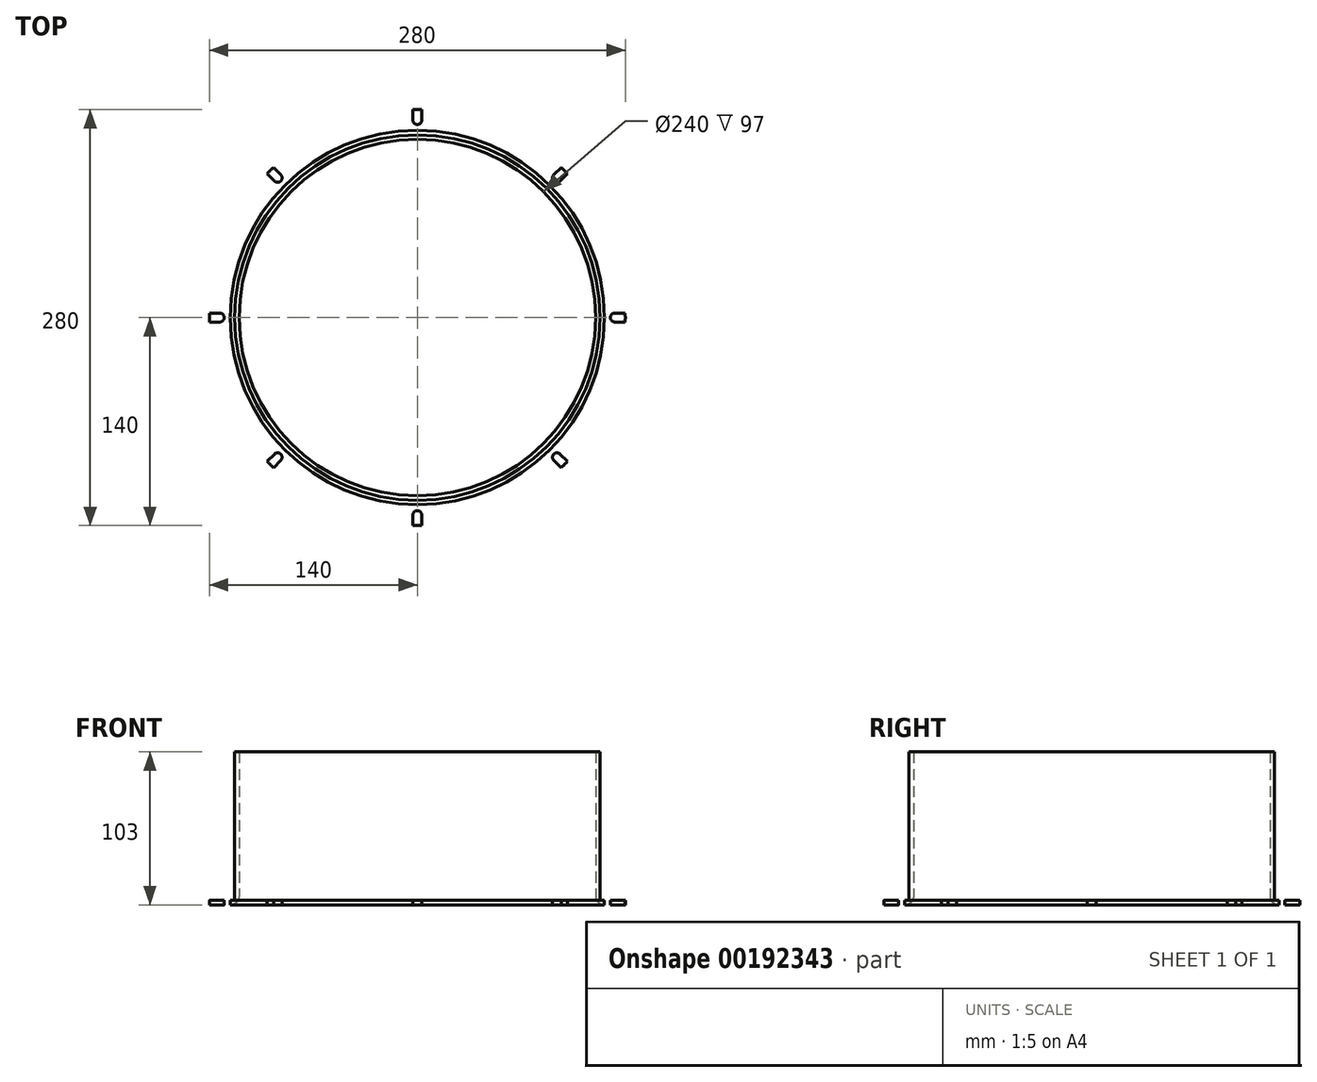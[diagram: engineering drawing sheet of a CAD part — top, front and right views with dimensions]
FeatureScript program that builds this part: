
annotation { "Feature Type Name" : "Feature", "Feature Type Description" : "" }
export const myFeature = defineFeature(function(context is Context, id is Id, definition is map)
    precondition{}
    {
        {
            var Q0;
            Q0=qCreatedBy(makeId("Top.planeOp"),FACE);
            var sketch = newSketch(context, id + "F0", { "sketchPlane" : qUnion([Q0])});
            skCircle(sketch, "E0", {"center": v(0, 0) * mm, "radius": 140 * mm});
            skCircle(sketch, "E1.0", {"center": v(0, 0) * mm, "radius": 120 * mm});
            skSolve(sketch);
        }
        {
            var Q0;
            Q0=makeQuery(id+"F0.imprint","IMPRINT",FACE,{"disambiguationData":[TD([[makeQuery(id+"F0.imprint","IMPRINT",EDGE,{"derivedFrom":sQuery(id+"F0.wireOp",EDGE,"E0")}),1.0]])]});
            extrude(context, id + "F1", {"entities" : qUnion([Q0]), "depth" : 3 * mm});
        }
        {
            var Q0;
            Q0=makeQuery(id+"F1.opExtrude","CAP_FACE",FACE,{"disambiguationData":[OSD([sQuery(id+"F0.wireOp",EDGE,"E0"),sQuery(id+"F0.wireOp",EDGE,"E1.0")])],"isStart":false});
            var sketch = newSketch(context, id + "F2", { "sketchPlane" : qUnion([Q0])});
            skCircle(sketch, "E2.0", {"center": v(0, 0) * mm, "radius": 120 * mm});
            skCircle(sketch, "E3.0", {"center": v(0, 0) * mm, "radius": 123 * mm});
            skSolve(sketch);
        }
        {
            var Q0;
            Q0=makeQuery(id+"F2.imprint","IMPRINT",FACE,{"disambiguationData":[TD([[makeQuery(id+"F2.imprint","IMPRINT",EDGE,{"derivedFrom":sQuery(id+"F2.wireOp",EDGE,"E2.0")}),-1.0]])]});
            extrude(context, id + "F3", {"entities" : qUnion([Q0]), "operationType" : NewBodyOperationType.ADD, "depth" : 100 * mm});
        }
        {
            var Q0;
            Q0=makeQuery(id+"F1.opExtrude","CAP_EDGE",EDGE,{"disambiguationData":[OSD([sQuery(id+"F0.wireOp",EDGE,"E1.0")])],"isStart":true});
            fillet(context, id + "F4", {"entities" : qUnion([Q0]), "radius" : 6 * mm, "tangentPropagation" : true, "allowEdgeOverflow" : false});
        }
        {
            var Q0;
            Q0=makeQuery(id+"F1.opExtrude","CAP_FACE",FACE,{"disambiguationData":[OSD([sQuery(id+"F0.wireOp",EDGE,"E0"),sQuery(id+"F0.wireOp",EDGE,"E1.0")])],"isStart":false});
            var sketch = newSketch(context, id + "F5", { "sketchPlane" : qUnion([Q0])});
            skCircle(sketch, "E4.0.0", {"center": v(0, 0) * mm, "radius": 140 * mm});
            skLineSegment(sketch, "E5", {"start": v(0, -140) * mm, "end": v(0, -133) * mm});
            skArc(sketch, "E6.0.startCap", {"start": v(3, -140) * mm, "mid": v(0, -143) * mm, "end": v(-3, -140) * mm});
            skArc(sketch, "E6.0.endCap", {"start": v(-3, -133) * mm, "mid": v(0, -130) * mm, "end": v(3, -133) * mm});
            skLineSegment(sketch, "E6.0.left", {"start": v(-3, -140) * mm, "end": v(-3, -133) * mm});
            skLineSegment(sketch, "E6.0.right", {"start": v(3, -140) * mm, "end": v(3, -133) * mm});
            skCircle(sketch, "E7.0", {"center": v(0, 0) * mm, "radius": 126 * mm});
            skArc(sketch, "E8.1.0", {"start": v(101.12, -96.87) * mm, "mid": v(101.12, -101.12) * mm, "end": v(96.87, -101.12) * mm});
            skLineSegment(sketch, "E8.1.1", {"start": v(96.87, -101.12) * mm, "end": v(91.92, -96.17) * mm});
            skLineSegment(sketch, "E8.1.2", {"start": v(101.12, -96.87) * mm, "end": v(96.17, -91.92) * mm});
            skArc(sketch, "E8.1.3", {"start": v(91.92, -96.17) * mm, "mid": v(91.92, -91.92) * mm, "end": v(96.17, -91.92) * mm});
            skArc(sketch, "E8.2.0", {"start": v(140, 3) * mm, "mid": v(143, 0) * mm, "end": v(140, -3) * mm});
            skLineSegment(sketch, "E8.2.1", {"start": v(140, -3) * mm, "end": v(133, -3) * mm});
            skLineSegment(sketch, "E8.2.2", {"start": v(140, 3) * mm, "end": v(133, 3) * mm});
            skArc(sketch, "E8.2.3", {"start": v(133, -3) * mm, "mid": v(130, 0) * mm, "end": v(133, 3) * mm});
            skArc(sketch, "E8.3.0", {"start": v(96.87, 101.12) * mm, "mid": v(101.12, 101.12) * mm, "end": v(101.12, 96.87) * mm});
            skLineSegment(sketch, "E8.3.1", {"start": v(101.12, 96.87) * mm, "end": v(96.17, 91.92) * mm});
            skLineSegment(sketch, "E8.3.2", {"start": v(96.87, 101.12) * mm, "end": v(91.92, 96.17) * mm});
            skArc(sketch, "E8.3.3", {"start": v(96.17, 91.92) * mm, "mid": v(91.92, 91.92) * mm, "end": v(91.92, 96.17) * mm});
            skArc(sketch, "E8.4.0", {"start": v(-3, 140) * mm, "mid": v(0, 143) * mm, "end": v(3, 140) * mm});
            skLineSegment(sketch, "E8.4.1", {"start": v(3, 140) * mm, "end": v(3, 133) * mm});
            skLineSegment(sketch, "E8.4.2", {"start": v(-3, 140) * mm, "end": v(-3, 133) * mm});
            skArc(sketch, "E8.4.3", {"start": v(3, 133) * mm, "mid": v(0, 130) * mm, "end": v(-3, 133) * mm});
            skArc(sketch, "E8.5.0", {"start": v(-101.12, 96.87) * mm, "mid": v(-101.12, 101.12) * mm, "end": v(-96.87, 101.12) * mm});
            skLineSegment(sketch, "E8.5.1", {"start": v(-96.87, 101.12) * mm, "end": v(-91.92, 96.17) * mm});
            skLineSegment(sketch, "E8.5.2", {"start": v(-101.12, 96.87) * mm, "end": v(-96.17, 91.92) * mm});
            skArc(sketch, "E8.5.3", {"start": v(-91.92, 96.17) * mm, "mid": v(-91.92, 91.92) * mm, "end": v(-96.17, 91.92) * mm});
            skArc(sketch, "E8.6.0", {"start": v(-140, -3) * mm, "mid": v(-143, 0) * mm, "end": v(-140, 3) * mm});
            skLineSegment(sketch, "E8.6.1", {"start": v(-140, 3) * mm, "end": v(-133, 3) * mm});
            skLineSegment(sketch, "E8.6.2", {"start": v(-140, -3) * mm, "end": v(-133, -3) * mm});
            skArc(sketch, "E8.6.3", {"start": v(-133, 3) * mm, "mid": v(-130, 0) * mm, "end": v(-133, -3) * mm});
            skArc(sketch, "E8.7.0", {"start": v(-96.87, -101.12) * mm, "mid": v(-101.12, -101.12) * mm, "end": v(-101.12, -96.87) * mm});
            skLineSegment(sketch, "E8.7.1", {"start": v(-101.12, -96.87) * mm, "end": v(-96.17, -91.92) * mm});
            skLineSegment(sketch, "E8.7.2", {"start": v(-96.87, -101.12) * mm, "end": v(-91.92, -96.17) * mm});
            skArc(sketch, "E8.7.3", {"start": v(-96.17, -91.92) * mm, "mid": v(-91.92, -91.92) * mm, "end": v(-91.92, -96.17) * mm});
            skSolve(sketch);
        }
        {
            var Q0;
            {var subQ5=sQuery(id+"F5.wireOp",EDGE,"E8.7.3");Q0=makeQuery(id+"F5.imprint","IMPRINT",FACE,{"disambiguationData":[TD([[makeQuery(id+"F5.imprint","IMPRINT",EDGE,{"derivedFrom":subQ5}),-1.0]])]});}
            var Q1;
            {var subQ1=sQuery(id+"F5.wireOp",EDGE,"E6.0.endCap");Q1=makeQuery(id+"F5.imprint","IMPRINT",FACE,{"disambiguationData":[TD([[makeQuery(id+"F5.imprint","IMPRINT",EDGE,{"derivedFrom":subQ1}),-1.0]])]});}
            var Q2;
            {var subQ5=sQuery(id+"F5.wireOp",EDGE,"E8.6.3");Q2=makeQuery(id+"F5.imprint","IMPRINT",FACE,{"disambiguationData":[TD([[makeQuery(id+"F5.imprint","IMPRINT",EDGE,{"derivedFrom":subQ5}),-1.0]])]});}
            var Q3;
            {var subQ5=sQuery(id+"F5.wireOp",EDGE,"E8.5.3");Q3=makeQuery(id+"F5.imprint","IMPRINT",FACE,{"disambiguationData":[TD([[makeQuery(id+"F5.imprint","IMPRINT",EDGE,{"derivedFrom":subQ5}),-1.0]])]});}
            var Q4;
            {var subQ5=sQuery(id+"F5.wireOp",EDGE,"E8.4.3");Q4=makeQuery(id+"F5.imprint","IMPRINT",FACE,{"disambiguationData":[TD([[makeQuery(id+"F5.imprint","IMPRINT",EDGE,{"derivedFrom":subQ5}),-1.0]])]});}
            var Q5;
            {var subQ5=sQuery(id+"F5.wireOp",EDGE,"E8.1.3");Q5=makeQuery(id+"F5.imprint","IMPRINT",FACE,{"disambiguationData":[TD([[makeQuery(id+"F5.imprint","IMPRINT",EDGE,{"derivedFrom":subQ5}),-1.0]])]});}
            var Q6;
            {var subQ5=sQuery(id+"F5.wireOp",EDGE,"E8.2.3");Q6=makeQuery(id+"F5.imprint","IMPRINT",FACE,{"disambiguationData":[TD([[makeQuery(id+"F5.imprint","IMPRINT",EDGE,{"derivedFrom":subQ5}),-1.0]])]});}
            var Q7;
            {var subQ5=sQuery(id+"F5.wireOp",EDGE,"E8.3.3");Q7=makeQuery(id+"F5.imprint","IMPRINT",FACE,{"disambiguationData":[TD([[makeQuery(id+"F5.imprint","IMPRINT",EDGE,{"derivedFrom":subQ5}),-1.0]])]});}
            extrude(context, id + "F6", {"entities" : qUnion([Q0, Q1, Q2, Q3, Q4, Q5, Q6, Q7]), "operationType" : NewBodyOperationType.REMOVE, "endBound" : BoundingType.THROUGH_ALL, "oppositeDirection" : true, "depth" : 25 * mm});
        }
    });
